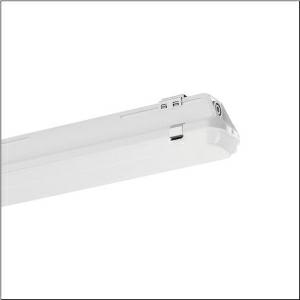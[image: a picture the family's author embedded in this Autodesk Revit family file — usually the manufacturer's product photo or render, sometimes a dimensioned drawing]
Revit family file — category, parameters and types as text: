
# Revit family: monsun_21_51fb207l440k
name_source: partatom
category: Lighting Fixtures
units: mm (PartAtom-declared; Revit-internal decimal feet)

## family parameters
Cut with Voids When Loaded = No
Host = Face
Light Source = No
Part Type = Normal
Room Calculation Point = No
Round Connector Dimension = Use Diameter
Shared = No

## types (1)
- Monsun 21 (1 x LED, 4330 lm, 27.2 W, 4000K)
    Apparent Load = 27 VA
    CIE Flux Codes = 45 75 93 94 100
    Color Rendering = 80
    Color Temperature = 4000K
    Default Elevation = 1800 mm
    Description = Monsun 21, damp-proof luminaire, chain hanger, primary optical cover: enclosure, of PC, light emission: direct distribution, primary light characteristic: symmetric, installation type: suspended mounting, surface-mounted, horizontal mounting, vertical mounting, LED, rated luminous flux: 4.330lm, luminous efficacy: 159lm/W, light colour: 840, colour temperature: 4000K, control gear: ON/OFF, with terminal, 3-pole, max. 2.5mm², mains connection: 220..240V, AC, 50/60Hz, rated input power: 27W, housing, of glass-fibre reinforced plastic, uncoated, bright grey, incl. chain hanger, length: 1.299mm, width: 90mm, height: 88mm, clip for enclosure, of stainless steel (V2A), ceiling mounting element, of stainless steel (V2A), chain hanger, of stainless steel (V2A), protection rating (complete): IP66, insulation class (complete): insulation class I (protective earthing), certification: CE, ENEC, VDE, UKCA, protection symbol: D, impact resistance: IK08, permissible operating ambient temperature: -25..+35°C, standard: EN 50419, EN 60598-2-1, corresponds to IFS (International Featured Standards) requirements for safety and quality in the food industry, for indoor or canopied outdoor use, no direct snow, no direct sun, no direct rain, LABS conformity tested according to VDMA 24364:2018-05, contact your sales advisor before using the luminaires in applications with unclear chemical exposure, large temperature fluctuations or condensation-forming humidity, packaging unit: 1 piece
    Height = 88 mm
    Lamp = 1 x LED
    Lamp Light Flux = 4330 lm
    Lamp Power = 27.2 W
    Lamp count = 1
    Length = 1299 mm
    Luminous efficacy = 159 lm/W
    Manufacturer = Siteco
    ModVariant = No
    Model = 51FB207L440K
    Mounting Place = Ceiling
    Mounting Type = Surface mounted
    Number of Poles = 1
    OnlyDefault = Yes
    Power Factor = 1
    Product Name = Monsun 21
    Product group = damp-proof luminaire
    ProductGroupID = 300
    Protection Class = Protection class I
    Protection Degree = IP 66
    RLX_Detail_Level = 1
    RLX_Emergency_Light_Flux = 0 lm
    RLX_Emergency_Type = 0
    RLX_Emergency_Type_DB = No
    RlxData = <blob elided: 89569 chars, md5=be0c0d2b>
    Socket = socket
    Standby Power = 0 W
    System Light Flux = 4330 lm
    System Power = 27 W
    Type Comments = Product without accessories
    Type Image = l_1319656.jpg
    URL = http://relux.com
    VarID = ---
    Voltage = 0 V
    Weight = 0.00 kg
    Width = 90 mm

## geometry (parser evidence)
native form markers: Blend x4, Sweep x15
no freeform markers — native parametric forms only
